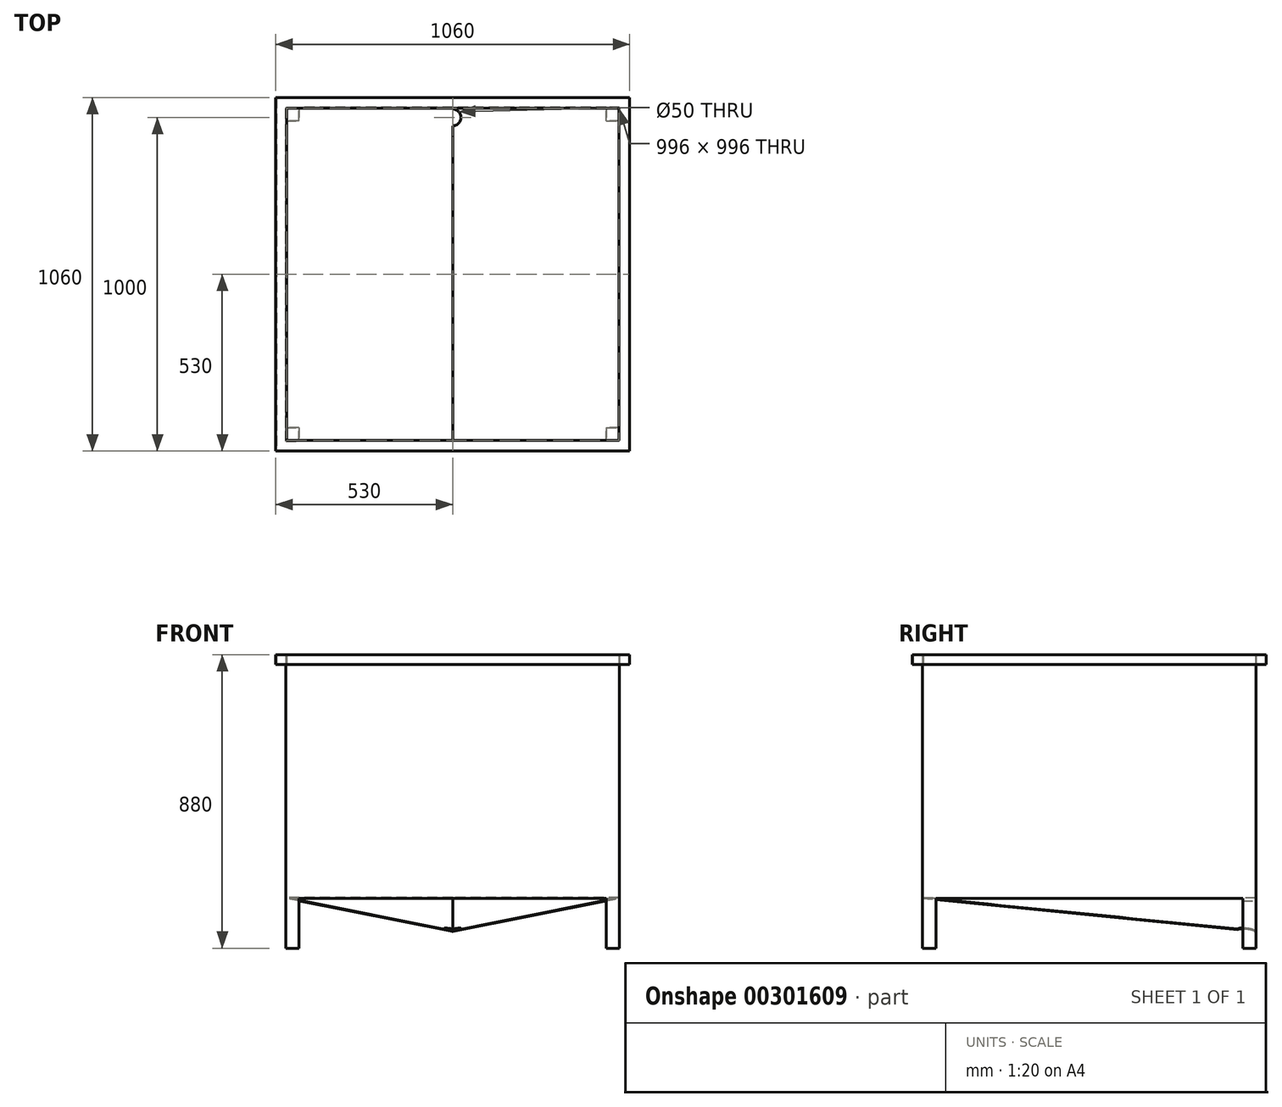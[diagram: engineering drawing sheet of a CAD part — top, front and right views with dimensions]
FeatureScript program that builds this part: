
annotation { "Feature Type Name" : "Feature", "Feature Type Description" : "" }
export const myFeature = defineFeature(function(context is Context, id is Id, definition is map)
    precondition{}
    {
        {
            var Q0;
            Q0=qCreatedBy(makeId("Front.planeOp"),FACE);
            var sketch = newSketch(context, id + "F0", { "sketchPlane" : qUnion([Q0])});
            skLineSegment(sketch, "E0", {"start": v(0, 0) * mm, "end": v(-500, 100) * mm});
            skLineSegment(sketch, "E1", {"start": v(-500, 100) * mm, "end": v(-500, 800) * mm});
            skLineSegment(sketch, "E2", {"start": v(-500, 800) * mm, "end": v(500, 800) * mm});
            skLineSegment(sketch, "E3", {"start": v(500, 800) * mm, "end": v(500, 100) * mm});
            skLineSegment(sketch, "E4", {"start": v(500, 100) * mm, "end": v(0, 0) * mm});
            skSolve(sketch);
        }
        {
            var Q0;
            Q0=makeQuery(id+"F0.imprint","IMPRINT",FACE,{"disambiguationData":[TD([[makeQuery(id+"F0.imprint","IMPRINT",EDGE,{"derivedFrom":sQuery(id+"F0.wireOp",EDGE,"E0")}),-1.0]])]});
            cPlane(context, id + "F1", {"entities" : qUnion([Q0]), "cplaneType" : CPlaneType.OFFSET, "offset" : 1000 * mm, "width" : 150 * mm, "height" : 150 * mm});
        }
        {
            var Q0;
            Q0=qCreatedBy(id+"F1.planeOp",FACE);
            var sketch = newSketch(context, id + "F2", { "sketchPlane" : qUnion([Q0])});
            skLineSegment(sketch, "E5.bottom", {"start": v(500, 100) * mm, "end": v(-500, 100) * mm});
            skLineSegment(sketch, "E5.top", {"start": v(500, 800) * mm, "end": v(-500, 800) * mm});
            skLineSegment(sketch, "E5.left", {"start": v(500, 100) * mm, "end": v(500, 800) * mm});
            skLineSegment(sketch, "E5.right", {"start": v(-500, 100) * mm, "end": v(-500, 800) * mm});
            skSolve(sketch);
        }
        {
            var Q0;
            Q0=makeQuery(id+"F2.imprint","IMPRINT",FACE,{"disambiguationData":[TD([[makeQuery(id+"F2.imprint","IMPRINT",EDGE,{"derivedFrom":sQuery(id+"F2.wireOp",EDGE,"E5.bottom")}),-1.0]])]});
            var Q1;
            Q1=makeQuery(id+"F0.imprint","IMPRINT",FACE,{"disambiguationData":[TD([[makeQuery(id+"F0.imprint","IMPRINT",EDGE,{"derivedFrom":sQuery(id+"F0.wireOp",EDGE,"E0")}),-1.0]])]});
            loft(context, id + "F3", {"sheetProfilesArray" : [{ "sheetProfileEntities" : qUnion([Q0]) }, { "sheetProfileEntities" : qUnion([Q1]) }]});
        }
        {
            var Q0;
            Q0=makeQuery(id+"F3.opLoft","SWEPT_FACE",FACE,{"disambiguationData":[OSD([sQuery(id+"F0.wireOp",EDGE,"E1"),sQuery(id+"F0.wireOp",EDGE,"E2"),sQuery(id+"F0.wireOp",EDGE,"E3"),sQuery(id+"F2.wireOp",EDGE,"E5.top"),sQuery(id+"F2.wireOp",EDGE,"E5.left"),sQuery(id+"F2.wireOp",EDGE,"E5.right")])]});
            shell(context, id + "F4", {"entities" : qUnion([Q0]), "thickness" : 2 * mm});
        }
        {
            var Q0;
            Q0=qCreatedBy(makeId("Top.planeOp"),FACE);
            var sketch = newSketch(context, id + "F5", { "sketchPlane" : qUnion([Q0])});
            skLineSegment(sketch, "E6.bottom", {"start": v(-500, 0) * mm, "end": v(-460, 0) * mm});
            skLineSegment(sketch, "E6.top", {"start": v(-500, -40) * mm, "end": v(-460, -40) * mm});
            skLineSegment(sketch, "E6.left", {"start": v(-500, 0) * mm, "end": v(-500, -40) * mm});
            skLineSegment(sketch, "E6.right", {"start": v(-460, 0) * mm, "end": v(-460, -40) * mm});
            skLineSegment(sketch, "E7.bottom", {"start": v(500, 0) * mm, "end": v(460, 0) * mm});
            skLineSegment(sketch, "E7.top", {"start": v(500, -40) * mm, "end": v(460, -40) * mm});
            skLineSegment(sketch, "E7.left", {"start": v(500, 0) * mm, "end": v(500, -40) * mm});
            skLineSegment(sketch, "E7.right", {"start": v(460, 0) * mm, "end": v(460, -40) * mm});
            skLineSegment(sketch, "E8.bottom", {"start": v(-500, -1000) * mm, "end": v(-460, -1000) * mm});
            skLineSegment(sketch, "E8.top", {"start": v(-500, -960) * mm, "end": v(-460, -960) * mm});
            skLineSegment(sketch, "E8.left", {"start": v(-500, -1000) * mm, "end": v(-500, -960) * mm});
            skLineSegment(sketch, "E8.right", {"start": v(-460, -1000) * mm, "end": v(-460, -960) * mm});
            skLineSegment(sketch, "E9.bottom", {"start": v(500, -1000) * mm, "end": v(460, -1000) * mm});
            skLineSegment(sketch, "E9.top", {"start": v(500, -960) * mm, "end": v(460, -960) * mm});
            skLineSegment(sketch, "E9.left", {"start": v(500, -1000) * mm, "end": v(500, -960) * mm});
            skLineSegment(sketch, "E9.right", {"start": v(460, -1000) * mm, "end": v(460, -960) * mm});
            skSolve(sketch);
        }
        {
            var Q0;
            Q0 = qSketchRegion(id + "F5", true);
            extrude(context, id + "F6", {"entities" : qUnion([Q0]), "operationType" : NewBodyOperationType.ADD, "endBound" : BoundingType.UP_TO_NEXT, "depth" : 25 * mm, "hasSecondDirection" : true, "secondDirectionOppositeDirection" : true, "secondDirectionDepth" : 50 * mm});
        }
        {
            var Q0;
            Q0=qCreatedBy(makeId("Top.planeOp"),FACE);
            var sketch = newSketch(context, id + "F7", { "sketchPlane" : qUnion([Q0])});
            skCircle(sketch, "E10", {"center": v(0, -30) * mm, "radius": 25 * mm});
            skSolve(sketch);
        }
        {
            var Q0;
            Q0 = qSketchRegion(id + "F7", true);
            extrude(context, id + "F8", {"entities" : qUnion([Q0]), "operationType" : NewBodyOperationType.REMOVE, "endBound" : BoundingType.THROUGH_ALL, "depth" : 25 * mm});
        }
        {
            var Q0;
            Q0=makeQuery(id+"F3.opLoft","SWEPT_FACE",FACE,{"disambiguationData":[OSD([sQuery(id+"F0.wireOp",EDGE,"E1"),sQuery(id+"F0.wireOp",EDGE,"E2"),sQuery(id+"F0.wireOp",EDGE,"E3"),sQuery(id+"F2.wireOp",EDGE,"E5.top"),sQuery(id+"F2.wireOp",EDGE,"E5.left"),sQuery(id+"F2.wireOp",EDGE,"E5.right")])]});
            var sketch = newSketch(context, id + "F9", { "sketchPlane" : qUnion([Q0])});
            skLineSegment(sketch, "E11.bottom", {"start": v(-530, 30) * mm, "end": v(530, 30) * mm});
            skLineSegment(sketch, "E11.top", {"start": v(-530, -1030) * mm, "end": v(530, -1030) * mm});
            skLineSegment(sketch, "E11.left", {"start": v(-530, 30) * mm, "end": v(-530, -1030) * mm});
            skLineSegment(sketch, "E11.right", {"start": v(530, 30) * mm, "end": v(530, -1030) * mm});
            skLineSegment(sketch, "E12.bottom", {"start": v(498, -998) * mm, "end": v(-498, -998) * mm});
            skLineSegment(sketch, "E12.top", {"start": v(498, -2) * mm, "end": v(-498, -2) * mm});
            skLineSegment(sketch, "E12.left", {"start": v(498, -998) * mm, "end": v(498, -2) * mm});
            skLineSegment(sketch, "E12.right", {"start": v(-498, -998) * mm, "end": v(-498, -2) * mm});
            skSolve(sketch);
        }
        {
            var Q0;
            Q0 = qSketchRegion(id + "F9", true);
            extrude(context, id + "F10", {"entities" : qUnion([Q0]), "depth" : 30 * mm});
        }
        {
            var Q0;
            Q0=makeQuery(id+"F10.opExtrude","CAP_FACE",FACE,{"disambiguationData":[OSD([sQuery(id+"F9.wireOp",EDGE,"FndZbQnf-81JI-HG8c-Q8P9-2KPKVJcUPGay.bottom"),sQuery(id+"F9.wireOp",EDGE,"FndZbQnf-81JI-HG8c-Q8P9-2KPKVJcUPGay.top"),sQuery(id+"F9.wireOp",EDGE,"FndZbQnf-81JI-HG8c-Q8P9-2KPKVJcUPGay.left"),sQuery(id+"F9.wireOp",EDGE,"FndZbQnf-81JI-HG8c-Q8P9-2KPKVJcUPGay.right"),sQuery(id+"F9.wireOp",EDGE,"E11.bottom"),sQuery(id+"F9.wireOp",EDGE,"E11.top"),sQuery(id+"F9.wireOp",EDGE,"E11.left"),sQuery(id+"F9.wireOp",EDGE,"E11.right")])],"isStart":true});
            shell(context, id + "F11", {"entities" : qUnion([Q0]), "thickness" : 2 * mm});
        }
    });
